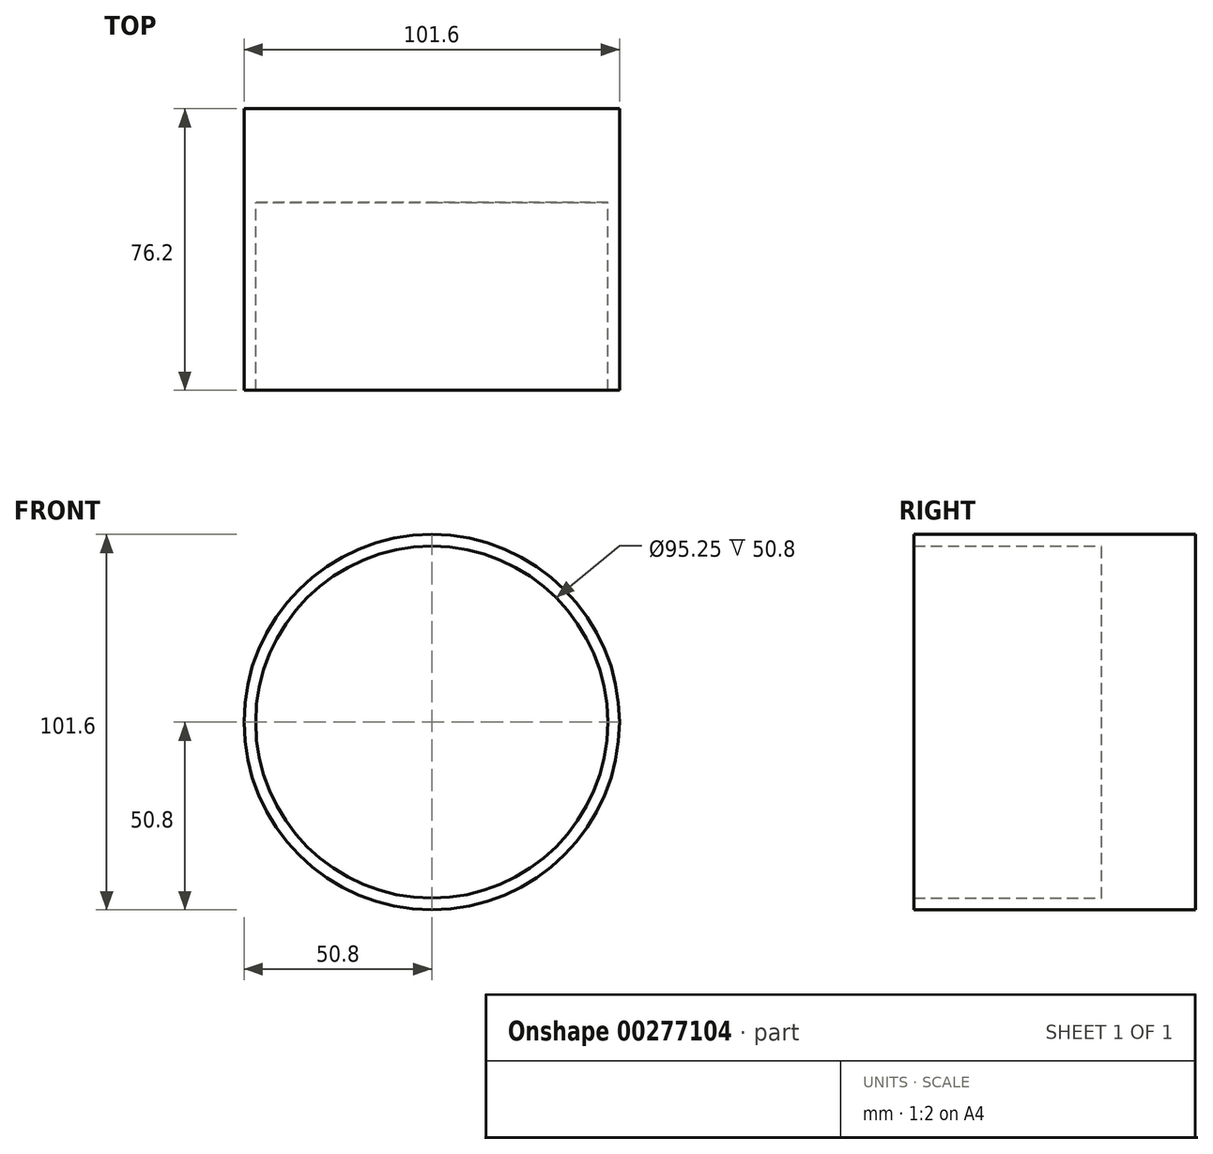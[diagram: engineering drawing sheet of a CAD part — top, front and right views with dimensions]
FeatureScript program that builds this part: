
annotation { "Feature Type Name" : "Feature", "Feature Type Description" : "" }
export const myFeature = defineFeature(function(context is Context, id is Id, definition is map)
    precondition{}
    {
        {
            var Q0;
            Q0=qCreatedBy(makeId("Front.planeOp"),FACE);
            var sketch = newSketch(context, id + "F0", { "sketchPlane" : qUnion([Q0])});
            skCircle(sketch, "E0", {"center": v(0, 0) * mm, "radius": 50.8 * mm});
            skCircle(sketch, "E1", {"center": v(0, 0) * mm, "radius": 47.63 * mm});
            skSolve(sketch);
        }
        {
            var Q0;
            Q0 = qSketchRegion(id + "F0", true);
            extrude(context, id + "F1", {"entities" : qUnion([Q0]), "depth" : 76.2 * mm});
        }
        {
            var Q0;
            Q0=makeQuery(id+"F0.imprint","IMPRINT",FACE,{"disambiguationData":[TD([[makeQuery(id+"F0.imprint","IMPRINT",EDGE,{"derivedFrom":sQuery(id+"F0.wireOp",EDGE,"E1")}),1.0]])]});
            extrude(context, id + "F2", {"entities" : qUnion([Q0]), "operationType" : NewBodyOperationType.ADD, "depth" : 25.4 * mm});
        }
    });
